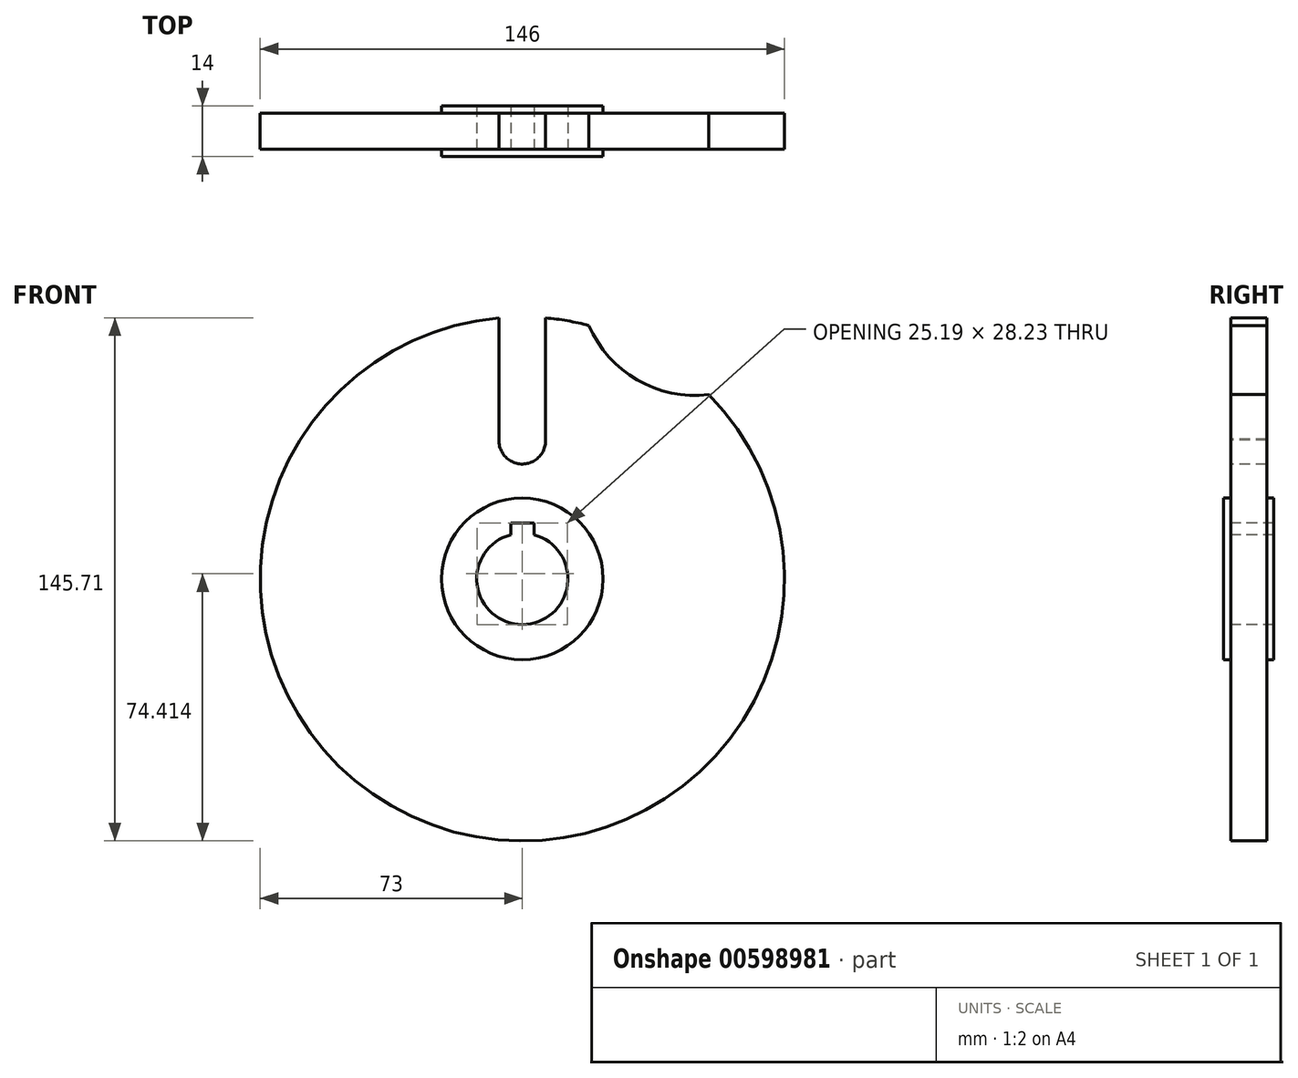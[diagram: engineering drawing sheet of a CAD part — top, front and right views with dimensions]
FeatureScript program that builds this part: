
annotation { "Feature Type Name" : "Feature", "Feature Type Description" : "" }
export const myFeature = defineFeature(function(context is Context, id is Id, definition is map)
    precondition{}
    {
        {
            var Q0;
            Q0=qCreatedBy(makeId("Front.planeOp"),FACE);
            var sketch = newSketch(context, id + "F0", { "sketchPlane" : qUnion([Q0])});
            skCircle(sketch, "E0", {"center": v(0, 0) * mm, "radius": 73 * mm});
            skLineSegment(sketch, "E1", {"start": v(0, 0) * mm, "end": v(0, 73) * mm, "construction": true});
            skCircle(sketch, "E2", {"center": v(0, 0) * mm, "radius": 38.5 * mm, "construction": true});
            skSolve(sketch);
        }
        {
            var Q0;
            Q0=qCreatedBy(makeId("Right.planeOp"),FACE);
            var sketch = newSketch(context, id + "F1", { "sketchPlane" : qUnion([Q0])});
            skLineSegment(sketch, "E3", {"start": v(10, 0) * mm, "end": v(-10, 0) * mm, "construction": true});
            skSolve(sketch);
        }
        {
            var Q0;
            Q0 = qSketchRegion(id + "F0", true);
            extrude(context, id + "F2", {"entities" : qUnion([Q0]), "endBound" : BoundingType.SYMMETRIC, "depth" : 10 * mm, "offsetDistance" : 25 * mm});
        }
        {
            var Q0;
            Q0=qCreatedBy(makeId("Front.planeOp"),FACE);
            var sketch = newSketch(context, id + "F3", { "sketchPlane" : qUnion([Q0])});
            skArc(sketch, "E4", {"start": v(-6.5, 38.69) * mm, "mid": v(0.12, 32) * mm, "end": v(6.49, 38.92) * mm});
            skLineSegment(sketch, "E5", {"start": v(-6.5, 38.69) * mm, "end": v(-6.5, 78.46) * mm});
            skLineSegment(sketch, "E6", {"start": v(6.49, 38.92) * mm, "end": v(6.49, 78.46) * mm});
            skLineSegment(sketch, "E7", {"start": v(-6.5, 78.46) * mm, "end": v(6.49, 78.46) * mm});
            skSolve(sketch);
        }
        {
            var Q0;
            Q0=makeQuery(id+"F3.imprint","IMPRINT",FACE,{"disambiguationData":[TD([[makeQuery(id+"F3.imprint","IMPRINT",EDGE,{"derivedFrom":sQuery(id+"F3.wireOp",EDGE,"E4")}),1.0]])]});
            extrude(context, id + "F4", {"entities" : qUnion([Q0]), "operationType" : NewBodyOperationType.REMOVE, "endBound" : BoundingType.THROUGH_ALL, "oppositeDirection" : true, "depth" : 25 * mm, "offsetDistance" : 25 * mm, "hasSecondDirection" : true, "secondDirectionBound" : SecondDirectionBoundingType.THROUGH_ALL, "secondDirectionOppositeDirection" : false, "secondDirectionDepth" : 25 * mm});
        }
        {
            var Q0;
            Q0=qCreatedBy(makeId("Front.planeOp"),FACE);
            var sketch = newSketch(context, id + "F5", { "sketchPlane" : qUnion([Q0])});
            skCircle(sketch, "E8", {"center": v(48, 83.14) * mm, "radius": 32 * mm});
            skLineSegment(sketch, "E9", {"start": v(0, 0) * mm, "end": v(48, 83.14) * mm, "construction": true});
            skSolve(sketch);
        }
        {
            var Q0;
            Q0 = qSketchRegion(id + "F5", true);
            extrude(context, id + "F6", {"entities" : qUnion([Q0]), "operationType" : NewBodyOperationType.REMOVE, "endBound" : BoundingType.THROUGH_ALL, "oppositeDirection" : true, "depth" : 25 * mm, "offsetDistance" : 25 * mm, "hasSecondDirection" : true, "secondDirectionBound" : SecondDirectionBoundingType.THROUGH_ALL, "secondDirectionOppositeDirection" : false, "secondDirectionDepth" : 25 * mm});
        }
        {
            var Q0;
            Q0=qCreatedBy(makeId("Front.planeOp"),FACE);
            var sketch = newSketch(context, id + "F7", { "sketchPlane" : qUnion([Q0])});
            skCircle(sketch, "E10", {"center": v(0, 0) * mm, "radius": 22.5 * mm});
            skSolve(sketch);
        }
        {
            var Q0;
            Q0 = qSketchRegion(id + "F7", true);
            extrude(context, id + "F8", {"entities" : qUnion([Q0]), "operationType" : NewBodyOperationType.ADD, "endBound" : BoundingType.SYMMETRIC, "depth" : 14 * mm, "offsetDistance" : 25 * mm});
        }
        {
            var Q0;
            Q0=qCreatedBy(makeId("Front.planeOp"),FACE);
            var sketch = newSketch(context, id + "F9", { "sketchPlane" : qUnion([Q0])});
            skArc(sketch, "E11", {"start": v(-3.25, 12.28) * mm, "mid": v(0, -12.7) * mm, "end": v(3.25, 12.28) * mm});
            skLineSegment(sketch, "E12.top", {"start": v(-3.25, 15.53) * mm, "end": v(3.25, 15.53) * mm});
            skLineSegment(sketch, "E12.left", {"start": v(-3.25, 12.28) * mm, "end": v(-3.25, 15.53) * mm});
            skLineSegment(sketch, "E12.right", {"start": v(3.25, 12.28) * mm, "end": v(3.25, 15.53) * mm});
            skPoint(sketch, "E13.orphan", {"position": v(-3.25, 0) * mm});
            skSolve(sketch);
        }
        {
            var Q0;
            Q0 = qSketchRegion(id + "F9", true);
            extrude(context, id + "F10", {"entities" : qUnion([Q0]), "operationType" : NewBodyOperationType.REMOVE, "endBound" : BoundingType.THROUGH_ALL, "oppositeDirection" : true, "depth" : 25 * mm, "offsetDistance" : 25 * mm, "hasSecondDirection" : true, "secondDirectionBound" : SecondDirectionBoundingType.THROUGH_ALL, "secondDirectionOppositeDirection" : false, "secondDirectionDepth" : 25 * mm});
        }
    });
